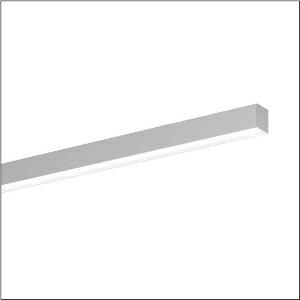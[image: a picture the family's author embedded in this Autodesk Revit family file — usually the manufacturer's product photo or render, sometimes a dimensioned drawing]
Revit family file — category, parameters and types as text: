
# Revit family: silica_21_51mx20tbt2s
name_source: partatom
category: Lighting Fixtures
units: mm (PartAtom-declared; Revit-internal decimal feet)

## family parameters
Cut with Voids When Loaded = No
Host = Face
Light Source = No
Part Type = Normal
Room Calculation Point = No
Round Connector Dimension = Use Diameter
Shared = No

## types (1)
- --- (1 x LED, 3000 lm, 25.6 W, 6500K)
    Apparent Load = 26 VA
    CIE Flux Codes = 48 79 96 100 100
    Color Rendering = 80
    Color Temperature = 6500K
    Default Elevation = 1800 mm
    Description = Silica 21, office luminaire, primary optical cover: cover, of PMMA, opal, light emission: direct distribution, primary light characteristic: symmetric, installation type: surface-mounted, LED, rated luminous flux: 3.000lm, luminous efficacy: 112lm/W, light colour: 8tw, colour temperature: 2700..6500K, control gear: DALI DT8, with terminal, 3+2-pole, max. 2.5mm², mains connection: 220..240V, AC, 50/60Hz, rated input power: 26.9W, luminaire housing, of aluminium, metallic grey (RAL 9006), length: 1.504mm, width: 53mm, height: 53mm, protection rating (complete): IP20, insulation class (complete): insulation class I (protective earthing), certification: CE, permissible operating ambient temperature: 0..+35°C, standard: EN 50419, packaging unit: 1 piece
    Height = 53 mm
    Lamp = 1 x LED
    Lamp Light Flux = 3000 lm
    Lamp Power = 25.6 W
    Lamp count = 1
    Length = 1504 mm
    Luminous efficacy = 117 lm/W
    Manufacturer = Siteco
    ModVariant = No
    Model = 51MX20TBT2S
    Mounting Place = Ceiling
    Mounting Type = Surface mounted
    Number of Poles = 1
    OnlyDefault = Yes
    Power Factor = 1
    Product Name = Silica 21
    Product group = office luminaire | ceiling mounted
    ProductGroupID = 301
    Protection Class = Protection class I
    Protection Degree = IP 20
    RLX_Detail_Level = 1
    RLX_Emergency_Light_Flux = 0 lm
    RLX_Emergency_Type = 0
    RLX_Emergency_Type_DB = No
    RlxData = <blob elided: 23157 chars, md5=553d0932>
    Socket = socket
    Standby Power = 0 W
    System Light Flux = 3000 lm
    System Power = 26 W
    Type Comments = individual setting
    Type Image = l_1335933.jpg
    URL = http://relux.com
    VarID = @adj_140719
    Voltage = 0 V
    Weight = 0.00 kg
    Width = 53 mm

## geometry (parser evidence)
native form markers: Blend x4, Sweep x12
no freeform markers — native parametric forms only
